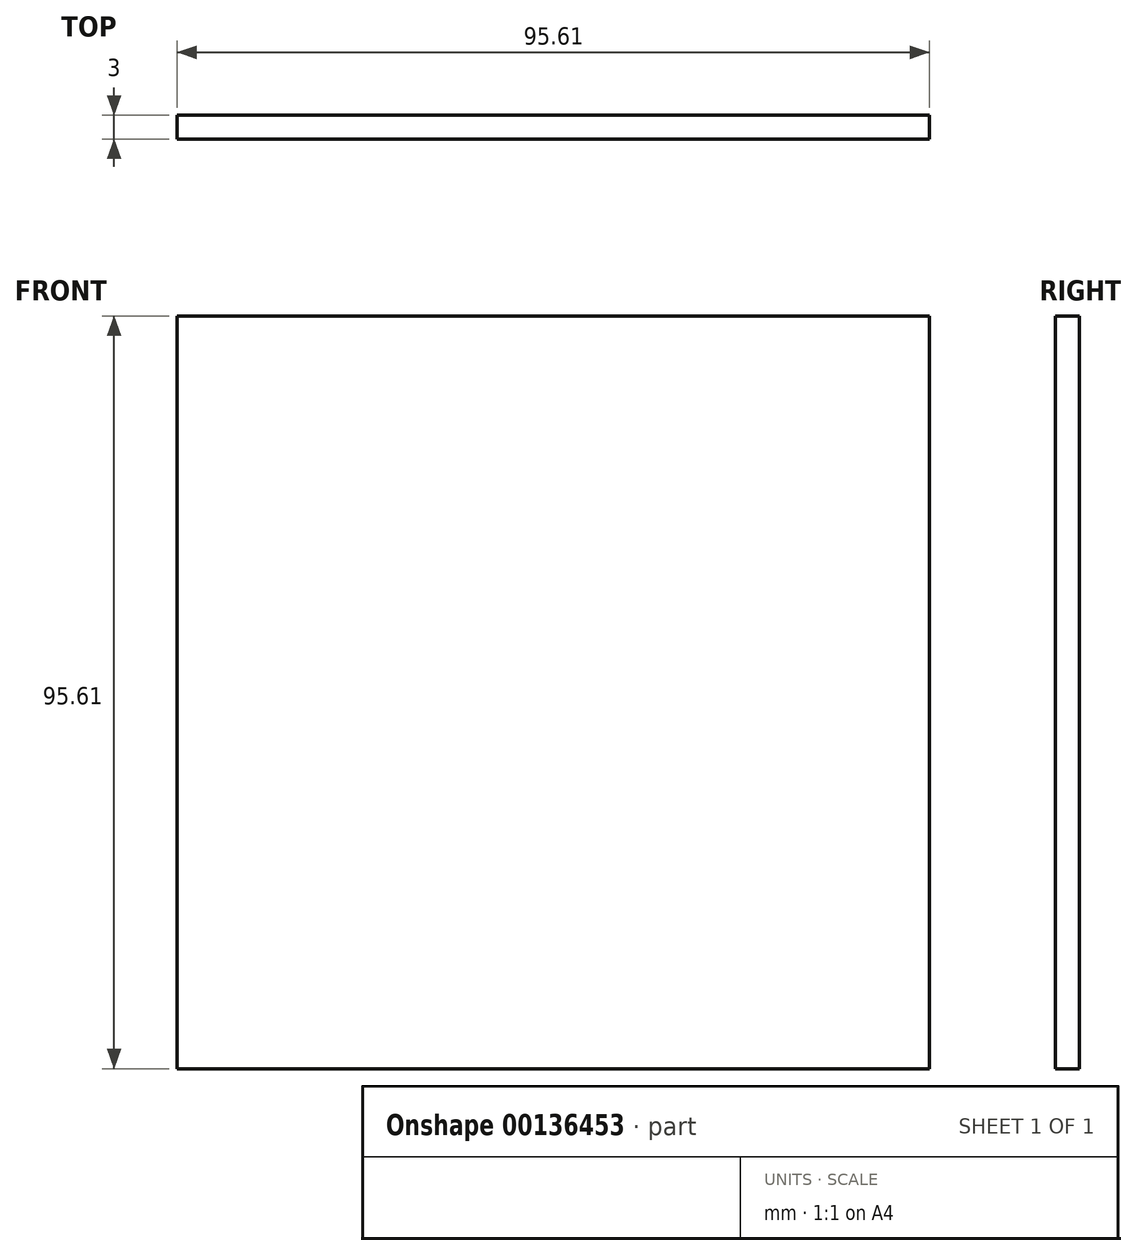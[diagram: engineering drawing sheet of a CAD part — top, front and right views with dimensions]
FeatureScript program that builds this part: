
annotation { "Feature Type Name" : "Feature", "Feature Type Description" : "" }
export const myFeature = defineFeature(function(context is Context, id is Id, definition is map)
    precondition{}
    {
        {
            var Q0;
            Q0=qCreatedBy(makeId("Front.planeOp"),FACE);
            var sketch = newSketch(context, id + "F0", { "sketchPlane" : qUnion([Q0])});
            skLineSegment(sketch, "E0.bottom", {"start": v(0, 0) * mm, "end": v(95.6, 0) * mm});
            skLineSegment(sketch, "E0.top", {"start": v(0, 95.6) * mm, "end": v(95.6, 95.6) * mm});
            skLineSegment(sketch, "E0.left", {"start": v(0, 0) * mm, "end": v(0, 95.6) * mm});
            skLineSegment(sketch, "E0.right", {"start": v(95.6, 0) * mm, "end": v(95.6, 95.6) * mm});
            skSolve(sketch);
        }
        {
            var Q0;
            Q0=makeQuery(id+"F0.imprint","IMPRINT",FACE,{"disambiguationData":[TD([[makeQuery(id+"F0.imprint","IMPRINT",EDGE,{"derivedFrom":sQuery(id+"F0.wireOp",EDGE,"E0.bottom")}),1.0]])]});
            extrude(context, id + "F1", {"entities" : qUnion([Q0]), "depth" : 3 * mm});
        }
    });
